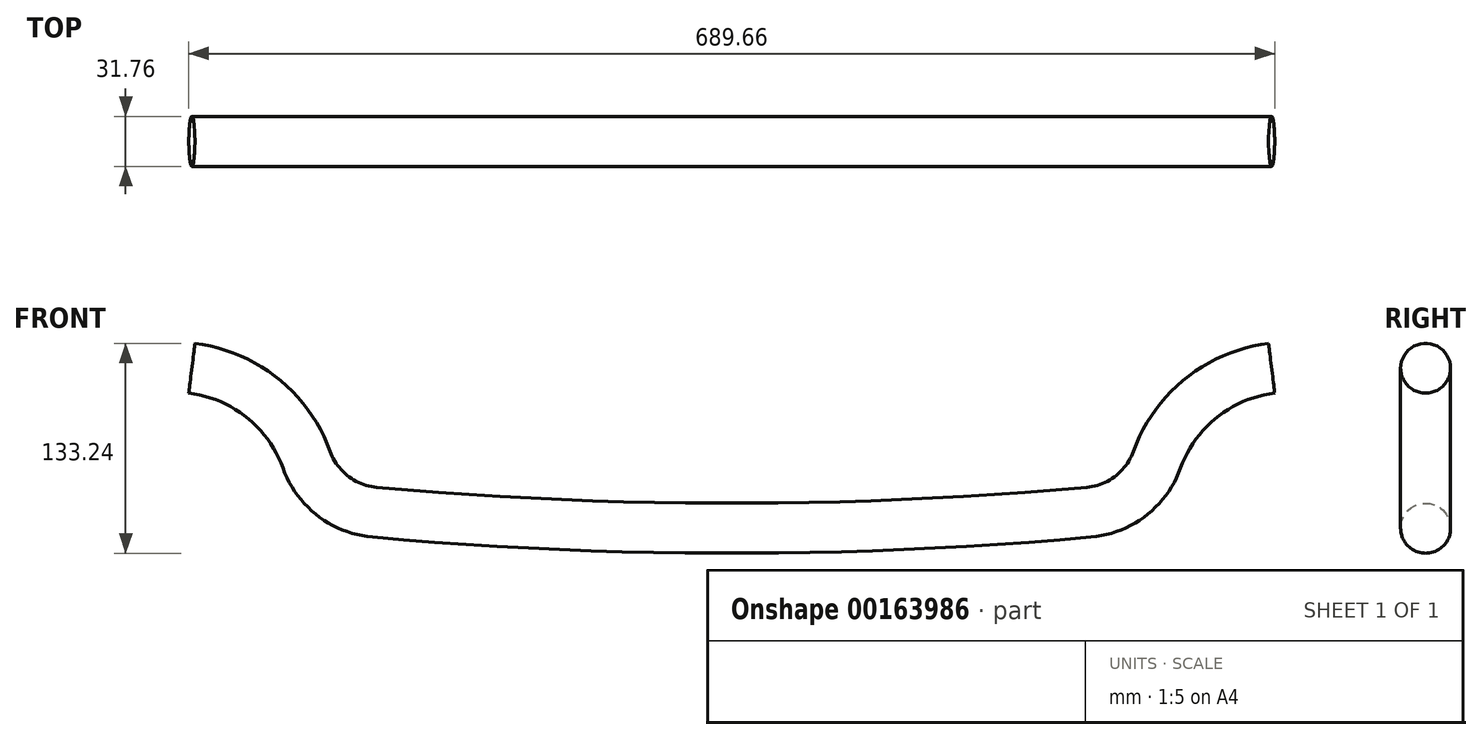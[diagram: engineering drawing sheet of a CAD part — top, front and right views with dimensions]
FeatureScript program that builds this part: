
annotation { "Feature Type Name" : "Feature", "Feature Type Description" : "" }
export const myFeature = defineFeature(function(context is Context, id is Id, definition is map)
    precondition{}
    {
        {
            var Q0;
            Q0=qCreatedBy(makeId("Front.planeOp"),FACE);
            var sketch = newSketch(context, id + "F0", { "sketchPlane" : qUnion([Q0])});
            skLineSegment(sketch, "E0.bottom", {"start": v(-342.9, 50.8) * mm, "end": v(342.9, 50.8) * mm, "construction": true});
            skLineSegment(sketch, "E0.top", {"start": v(-342.9, -50.8) * mm, "end": v(342.9, -50.8) * mm, "construction": true});
            skLineSegment(sketch, "E0.left", {"start": v(-342.9, 50.8) * mm, "end": v(-342.9, -50.8) * mm, "construction": true});
            skLineSegment(sketch, "E0.right", {"start": v(342.9, 50.8) * mm, "end": v(342.9, -50.8) * mm, "construction": true});
            skPoint(sketch, "E0.middle", {"position": v(0, 0) * mm});
            skLineSegment(sketch, "E1", {"start": v(0, -50.8) * mm, "end": v(0, 50.8) * mm, "construction": true});
            skLineSegment(sketch, "E2", {"start": v(-342.9, 50.8) * mm, "end": v(-355.37, -50.8) * mm, "construction": true});
            skArc(sketch, "E3", {"start": v(-226.85, -40.65) * mm, "mid": v(0, -50.8) * mm, "end": v(226.85, -40.65) * mm});
            skArc(sketch, "E4", {"start": v(-270.1, -7.28) * mm, "mid": v(-298.29, 32.05) * mm, "end": v(-342.9, 50.8) * mm});
            skPoint(sketch, "E5.visualSharp", {"position": v(-264.84, -36.96) * mm});
            skArc(sketch, "E5.filletArc", {"start": v(-270.1, -7.28) * mm, "mid": v(-253.35, -30.27) * mm, "end": v(-226.85, -40.65) * mm});
            skArc(sketch, "E6.MirrorCS", {"start": v(270.1, -7.28) * mm, "mid": v(298.29, 32.05) * mm, "end": v(342.9, 50.8) * mm});
            skArc(sketch, "E7.MirrorCS", {"start": v(270.1, -7.28) * mm, "mid": v(253.35, -30.27) * mm, "end": v(226.85, -40.65) * mm});
            skSolve(sketch);
        }
        {
            var Q0;
            Q0=qCreatedBy(makeId("Front.planeOp"),FACE);
            var Q1;
            Q1=sQuery(id+"F0.wireOp",EDGE,"E2");
            cPlane(context, id + "F1", {"entities" : qUnion([Q0, Q1]), "cplaneType" : CPlaneType.LINE_ANGLE, "offset" : 25.4 * mm, "angle" : 90 * degree, "width" : 152.4 * mm, "height" : 152.4 * mm});
        }
        {
            var Q0;
            Q0=qCreatedBy(id+"F1.planeOp",FACE);
            var sketch = newSketch(context, id + "F2", { "sketchPlane" : qUnion([Q0])});
            skCircle(sketch, "E8", {"center": v(0, 8.63) * mm, "radius": 15.88 * mm});
            skSolve(sketch);
        }
        {
            var Q0;
            Q0 = qSketchRegion(id + "F2", true);
            var Q1;
            Q1=sQuery(id+"F0.wireOp",EDGE,"E4");
            var Q2;
            Q2=sQuery(id+"F0.wireOp",EDGE,"E5.filletArc");
            var Q3;
            Q3=sQuery(id+"F0.wireOp",EDGE,"E3");
            var Q4;
            Q4=sQuery(id+"F0.wireOp",EDGE,"E7.MirrorCS");
            var Q5;
            Q5=sQuery(id+"F0.wireOp",EDGE,"E6.MirrorCS");
            sweep(context, id + "F3", {"profiles" : qUnion([Q0]), "path" : qUnion([Q1, Q2, Q3, Q4, Q5])});
        }
    });
